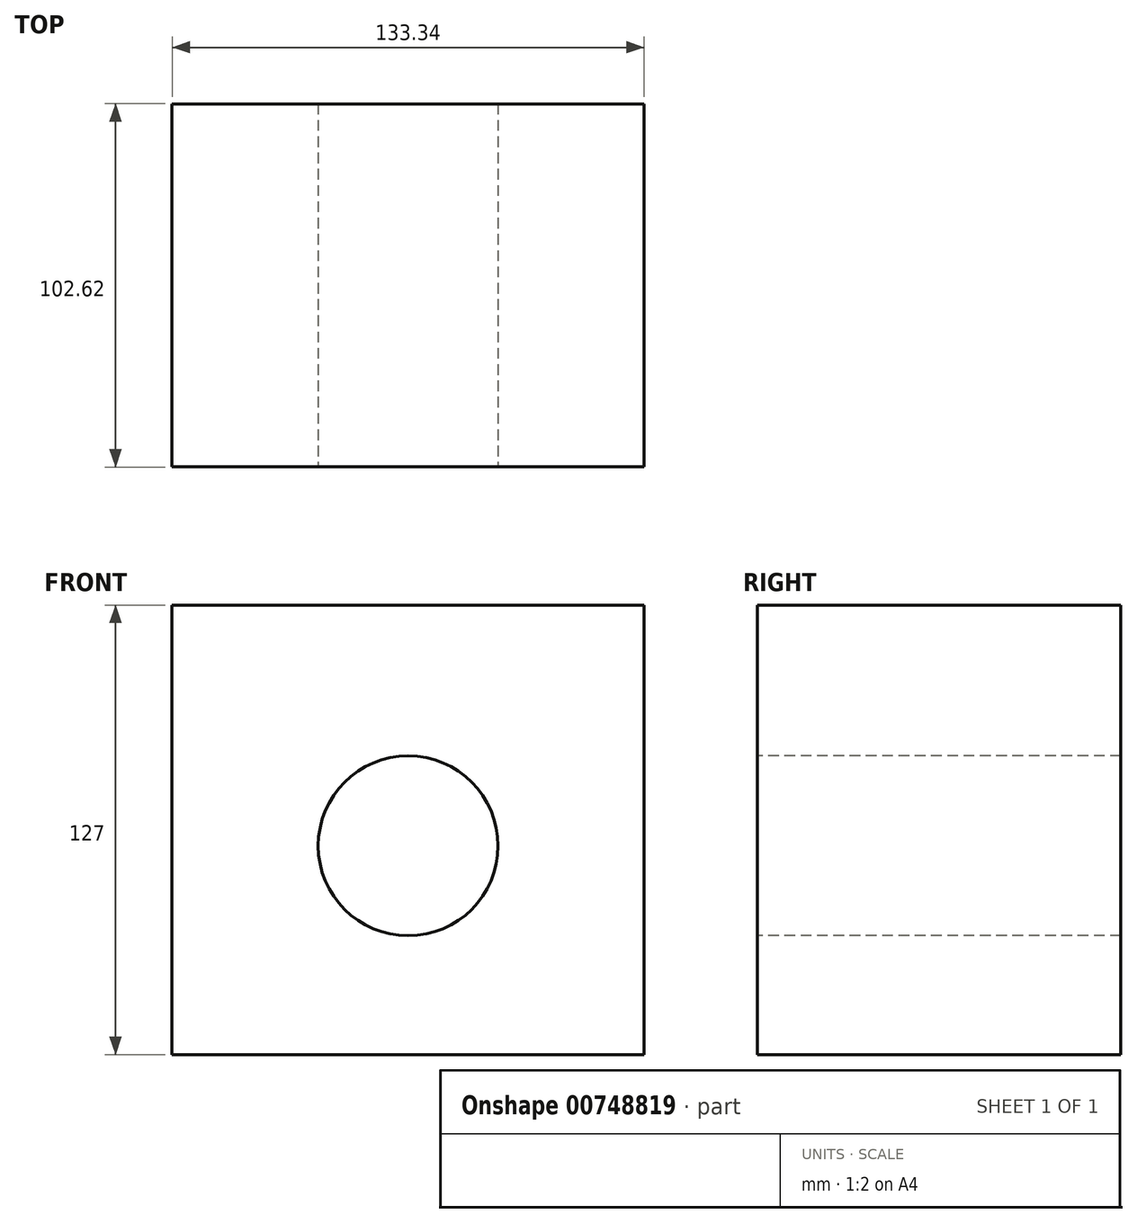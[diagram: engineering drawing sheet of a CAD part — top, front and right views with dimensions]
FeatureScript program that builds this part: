
annotation { "Feature Type Name" : "Feature", "Feature Type Description" : "" }
export const myFeature = defineFeature(function(context is Context, id is Id, definition is map)
    precondition{}
    {
        {
            var Q0;
            Q0=qCreatedBy(makeId("Top.planeOp"),FACE);
            var sketch = newSketch(context, id + "F0", { "sketchPlane" : qUnion([Q0])});
            skLineSegment(sketch, "E0.bottom", {"start": v(66.67, -25.78) * mm, "end": v(-66.67, -25.78) * mm});
            skLineSegment(sketch, "E0.top", {"start": v(66.67, 76.84) * mm, "end": v(-66.67, 76.84) * mm});
            skLineSegment(sketch, "E0.left", {"start": v(66.67, -25.78) * mm, "end": v(66.67, 76.84) * mm});
            skLineSegment(sketch, "E0.right", {"start": v(-66.67, -25.78) * mm, "end": v(-66.67, 76.84) * mm});
            skPoint(sketch, "E0.middle", {"position": v(0, 25.53) * mm});
            skSolve(sketch);
        }
        {
            var Q0;
            Q0 = qSketchRegion(id + "F0", true);
            extrude(context, id + "F1", {"entities" : qUnion([Q0]), "depth" : 127 * mm, "offsetDistance" : 25.4 * mm});
        }
        {
            var Q0;
            Q0=makeQuery(id+"F1.opExtrude","SWEPT_FACE",FACE,{"disambiguationData":[OSD([sQuery(id+"F0.wireOp",EDGE,"E0.bottom")])]});
            var sketch = newSketch(context, id + "F2", { "sketchPlane" : qUnion([Q0])});
            skPoint(sketch, "E1", {"position": v(0, 58.98) * mm});
            skSolve(sketch);
        }
        {
            var Q0;
            Q0=sQuery(id+"F2.wireOp",VERTEX,"E1");
            var Q1;
            Q1=makeQuery(id+"F1.opExtrude","SWEPT_BODY",BODY,{"disambiguationData":[OSD([sQuery(id+"F0.wireOp",EDGE,"E0.bottom"),sQuery(id+"F0.wireOp",EDGE,"E0.top"),sQuery(id+"F0.wireOp",EDGE,"E0.left"),sQuery(id+"F0.wireOp",EDGE,"E0.right")])]});
            hole(context, id + "F3", {"style" : HoleStyle.SIMPLE, "endStyle" : HoleEndStyle.THROUGH, "holeDiameter" : 50.8 * mm, "majorDiameter" : 6.35 * mm, "isTappedThrough" : true, "tappedDepth" : 12.7 * mm, "tapClearance" : 3, "locations" : qUnion([Q0]), "scope" : qUnion([Q1])});
        }
    });
